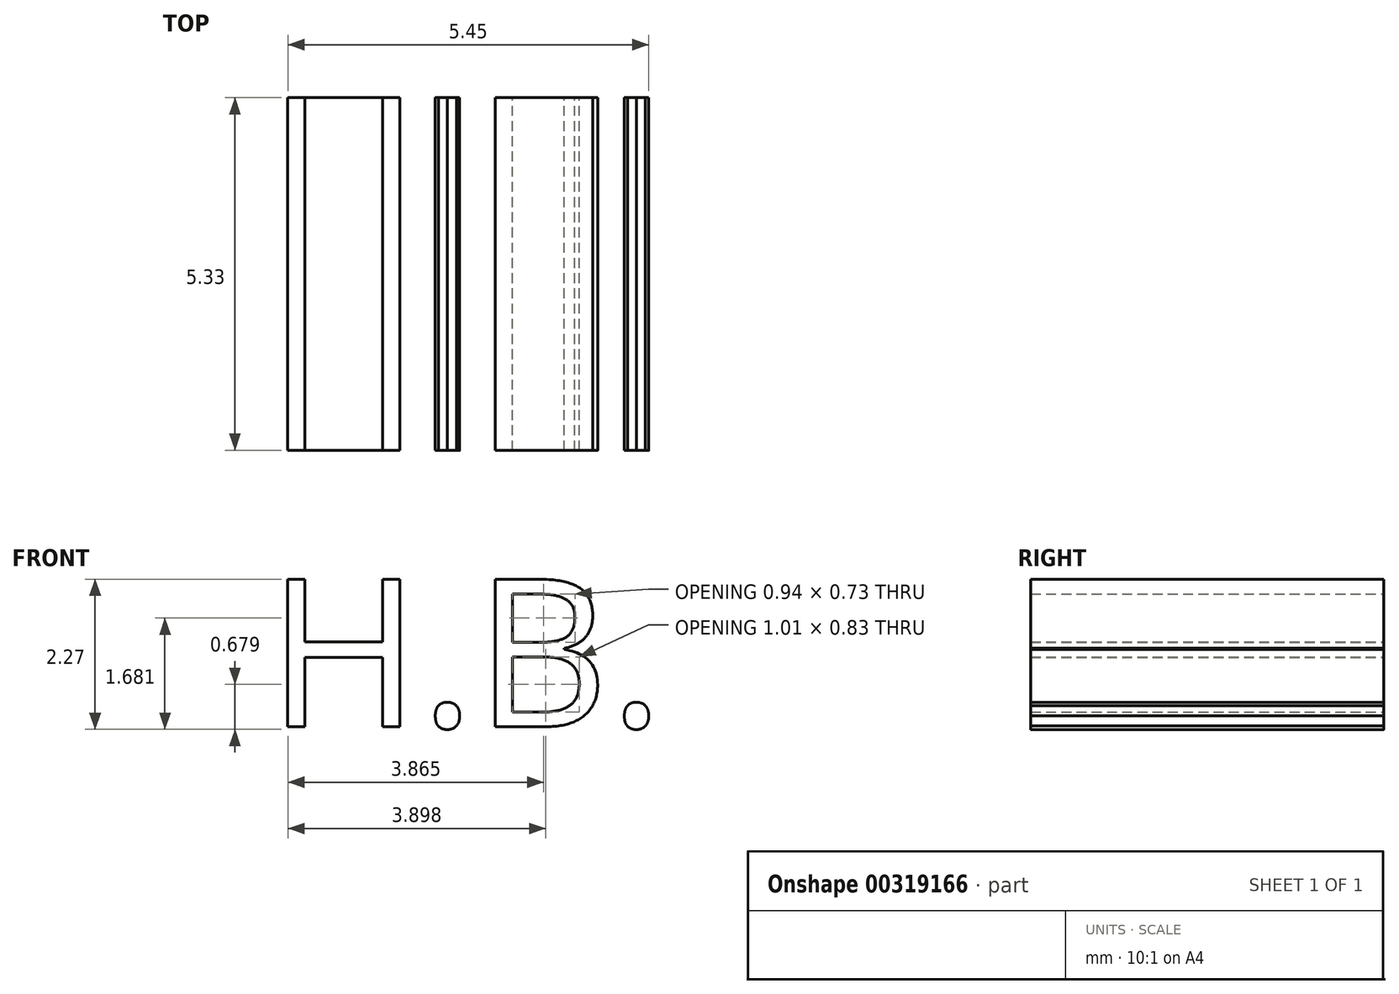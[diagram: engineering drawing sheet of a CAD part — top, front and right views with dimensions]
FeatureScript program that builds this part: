
annotation { "Feature Type Name" : "Feature", "Feature Type Description" : "" }
export const myFeature = defineFeature(function(context is Context, id is Id, definition is map)
    precondition{}
    {
        {
            var Q0;
            Q0=qCreatedBy(makeId("Front.planeOp"),FACE);
            var sketch = newSketch(context, id + "F0", { "sketchPlane" : qUnion([Q0])});
            skCircle(sketch, "E0", {"center": v(-59.35, 0) * mm, "radius": 12.7 * mm});
            skCircle(sketch, "E1.cCircle", {"center": v(-59.35, 0) * mm, "radius": 8.25 * mm, "construction": true});
            skLineSegment(sketch, "E1.0", {"start": v(-51.1, 3.42) * mm, "end": v(-51.1, -3.42) * mm});
            skLineSegment(sketch, "E1.1", {"start": v(-51.1, -3.42) * mm, "end": v(-55.93, -8.25) * mm});
            skLineSegment(sketch, "E1.2", {"start": v(-55.93, -8.25) * mm, "end": v(-62.77, -8.25) * mm});
            skLineSegment(sketch, "E1.3", {"start": v(-62.77, -8.25) * mm, "end": v(-67.6, -3.42) * mm});
            skLineSegment(sketch, "E1.4", {"start": v(-67.6, -3.42) * mm, "end": v(-67.6, 3.42) * mm});
            skLineSegment(sketch, "E1.5", {"start": v(-67.6, 3.42) * mm, "end": v(-62.77, 8.25) * mm});
            skLineSegment(sketch, "E1.6", {"start": v(-62.77, 8.25) * mm, "end": v(-55.93, 8.25) * mm});
            skLineSegment(sketch, "E1.7", {"start": v(-55.93, 8.25) * mm, "end": v(-51.1, 3.42) * mm});
            skPoint(sketch, "E1.0.midPoint", {"position": v(-51.1, 0) * mm});
            skArc(sketch, "E2", {"start": v(11.88, 12) * mm, "mid": v(-2.93, -6.93) * mm, "end": v(20.37, -1.05) * mm});
            skPoint(sketch, "E3.bottom.start.orphan", {"position": v(41.73, 0) * mm});
            skLineSegment(sketch, "E4", {"start": v(11.88, 12) * mm, "end": v(2.95, 5.66) * mm});
            skLineSegment(sketch, "E5", {"start": v(20.37, -1.05) * mm, "end": v(11.52, -6.35) * mm});
            skArc(sketch, "E6", {"start": v(2.95, 5.66) * mm, "mid": v(1.7, -4.3) * mm, "end": v(11.52, -6.35) * mm});
            skLineSegment(sketch, "E7.bottom", {"start": v(-41.96, 3.42) * mm, "end": v(-10.43, 3.42) * mm});
            skLineSegment(sketch, "E7.top", {"start": v(-41.96, -3.8) * mm, "end": v(-10.43, -3.8) * mm});
            skArc(sketch, "E8", {"start": v(-10.43, 3.42) * mm, "mid": v(-6.23, 4.37) * mm, "end": v(-2.85, 7.04) * mm});
            skArc(sketch, "E9", {"start": v(-3.13, -6.61) * mm, "mid": v(-6.52, -4.52) * mm, "end": v(-10.43, -3.8) * mm});
            skArc(sketch, "E10", {"start": v(-49.05, 7.43) * mm, "mid": v(-45.7, 5.07) * mm, "end": v(-41.96, 3.42) * mm});
            skArc(sketch, "E11", {"start": v(-41.96, -3.8) * mm, "mid": v(-45.8, -4.69) * mm, "end": v(-48.87, -7.18) * mm});
            skLineSegment(sketch, "E12.bottom", {"start": v(-39.38, 1.1) * mm, "end": v(-13.23, 1.1) * mm});
            skLineSegment(sketch, "E12.top", {"start": v(-39.38, -1.52) * mm, "end": v(-13.23, -1.52) * mm});
            skArc(sketch, "E13", {"start": v(-13.23, -1.52) * mm, "mid": v(-11.92, -0.21) * mm, "end": v(-13.23, 1.1) * mm});
            skArc(sketch, "E14", {"start": v(-39.38, 1.1) * mm, "mid": v(-40.7, -0.21) * mm, "end": v(-39.38, -1.52) * mm});
            skSolve(sketch);
        }
        {
            var Q0;
            Q0=makeQuery(id+"F0.imprint","IMPRINT",FACE,{"disambiguationData":[TD([[makeQuery(id+"F0.imprint","IMPRINT",EDGE,{"derivedFrom":sQuery(id+"F0.wireOp",EDGE,"E12.bottom")}),-1.0]])]});
            var sketch = newSketch(context, id + "F1", { "sketchPlane" : qUnion([Q0])});
            skText(sketch, "E15", { "text": "H.B.", "fontName": "OpenSans-Regular.ttf"});
            const initialGuessF1  = {"E15": [-0.02977, -0.0013, 1, 0, 0.00225]};
            skSetInitialGuess(sketch, initialGuessF1);
            skSolve(sketch);
        }
        {
            var Q0;
            Q0 = qSketchRegion(id + "F1", true);
            extrude(context, id + "F2", {"entities" : qUnion([Q0]), "depth" : 5.33 * mm});
        }
    });
